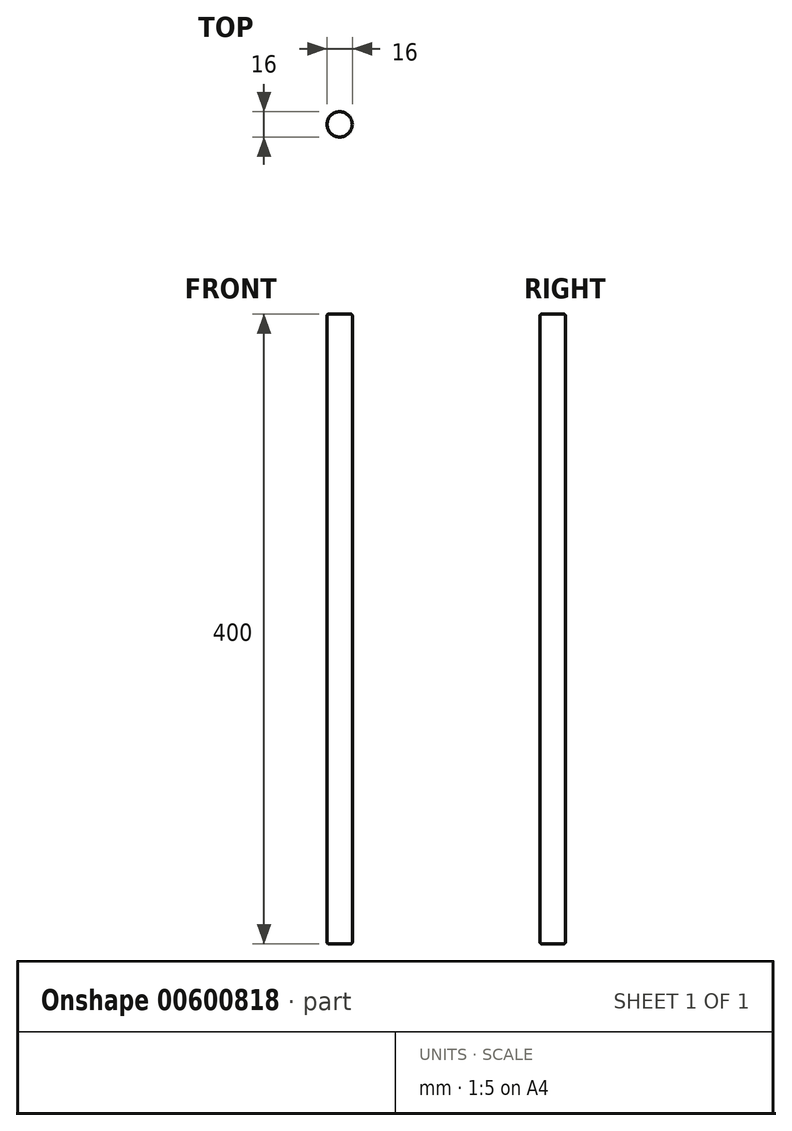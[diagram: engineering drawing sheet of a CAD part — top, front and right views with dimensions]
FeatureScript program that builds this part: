
annotation { "Feature Type Name" : "Feature", "Feature Type Description" : "" }
export const myFeature = defineFeature(function(context is Context, id is Id, definition is map)
    precondition{}
    {
        {
            var Q0;
            Q0=qCreatedBy(makeId("Top.planeOp"),FACE);
            var sketch = newSketch(context, id + "F0", { "sketchPlane" : qUnion([Q0])});
            skCircle(sketch, "E0", {"center": v(0, 0) * mm, "radius": 8 * mm});
            skSolve(sketch);
        }
        {
            var Q0;
            Q0 = qSketchRegion(id + "F0", true);
            extrude(context, id + "F1", {"entities" : qUnion([Q0]), "depth" : 400 * mm, "offsetDistance" : 25 * mm});
        }
        {
            var Q0;
            Q0=makeQuery(id+"F1.opExtrude","CAP_FACE",FACE,{"disambiguationData":[OSD([sQuery(id+"F0.wireOp",EDGE,"E0")])],"isStart":false});
            var Q1;
            Q1=makeQuery(id+"F1.opExtrude","CAP_EDGE",EDGE,{"disambiguationData":[OSD([sQuery(id+"F0.wireOp",EDGE,"E0")])],"isStart":true});
            fillet(context, id + "F2", {"entities" : qUnion([Q0, Q1]), "radius" : 1 * mm, "tangentPropagation" : true, "allowEdgeOverflow" : false});
        }
    });
